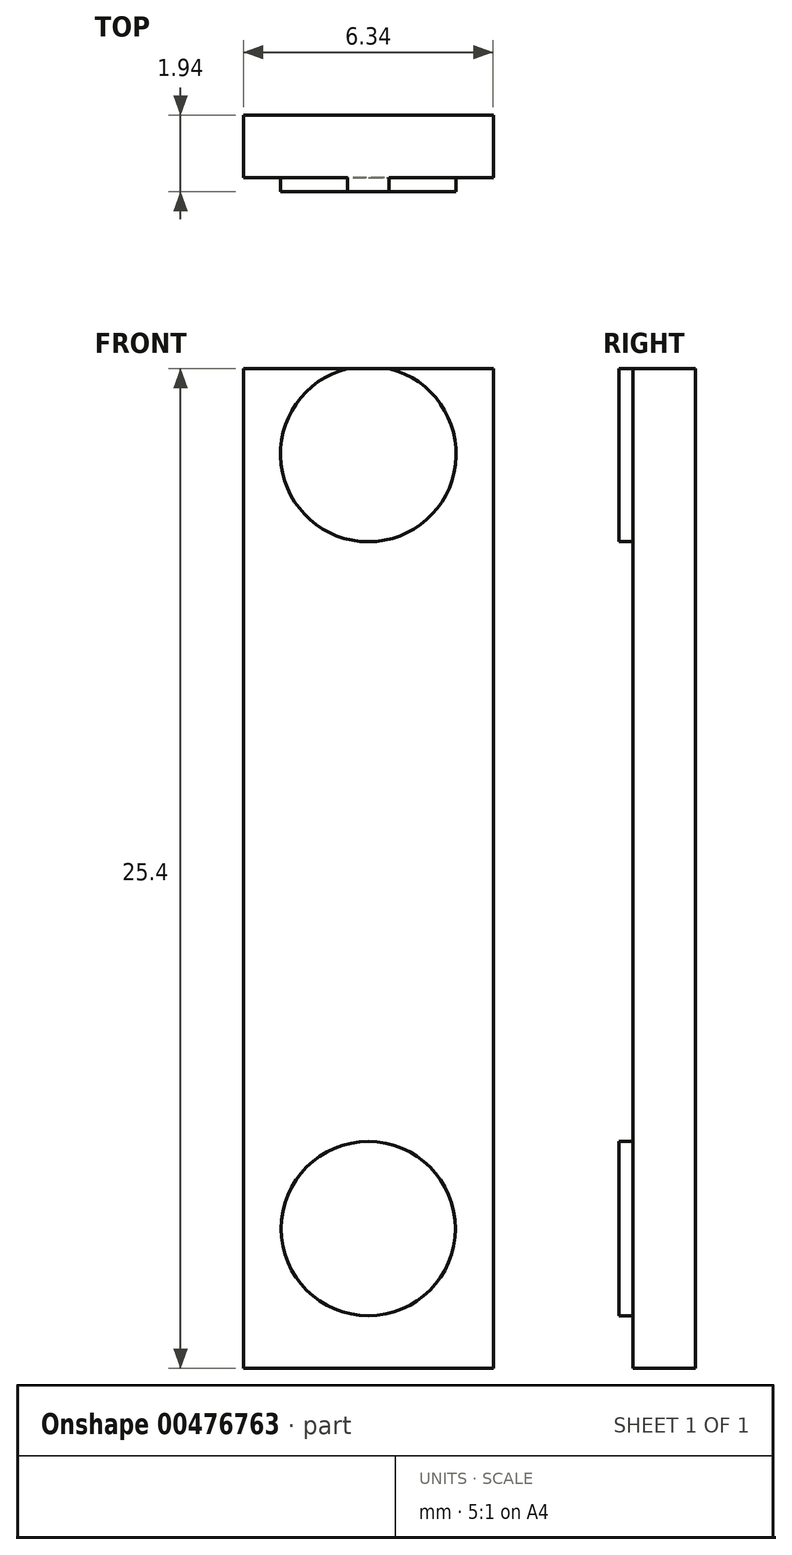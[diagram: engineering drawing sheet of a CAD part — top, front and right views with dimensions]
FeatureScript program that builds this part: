
annotation { "Feature Type Name" : "Feature", "Feature Type Description" : "" }
export const myFeature = defineFeature(function(context is Context, id is Id, definition is map)
    precondition{}
    {
        {
            var Q0;
            Q0=qCreatedBy(makeId("Front.planeOp"),FACE);
            var sketch = newSketch(context, id + "F0", { "sketchPlane" : qUnion([Q0])});
            skLineSegment(sketch, "E0.bottom", {"start": v(3.17, -12.7) * mm, "end": v(-3.18, -12.7) * mm});
            skLineSegment(sketch, "E0.top", {"start": v(3.18, 12.7) * mm, "end": v(-3.17, 12.7) * mm});
            skLineSegment(sketch, "E0.left", {"start": v(3.17, -12.7) * mm, "end": v(3.18, 12.7) * mm});
            skLineSegment(sketch, "E0.right", {"start": v(-3.18, -12.7) * mm, "end": v(-3.17, 12.7) * mm});
            skPoint(sketch, "E0.middle", {"position": v(0, 0) * mm});
            skSolve(sketch);
        }
        {
            var Q0;
            Q0=makeQuery(id+"F0.imprint","IMPRINT",FACE,{"disambiguationData":[TD([[makeQuery(id+"F0.imprint","IMPRINT",EDGE,{"derivedFrom":sQuery(id+"F0.wireOp",EDGE,"E0.bottom")}),-1.0]])]});
            extrude(context, id + "F1", {"entities" : qUnion([Q0]), "depth" : 1.59 * mm});
        }
        {
            var Q0;
            Q0=makeQuery(id+"F1.opExtrude","CAP_FACE",FACE,{"disambiguationData":[OSD([sQuery(id+"F0.wireOp",EDGE,"E0.bottom"),sQuery(id+"F0.wireOp",EDGE,"E0.top"),sQuery(id+"F0.wireOp",EDGE,"E0.left"),sQuery(id+"F0.wireOp",EDGE,"E0.right")])],"isStart":false});
            var sketch = newSketch(context, id + "F2", { "sketchPlane" : qUnion([Q0])});
            skCircle(sketch, "E1", {"center": v(0, -9.15) * mm, "radius": 2.21 * mm});
            skCircle(sketch, "E2", {"center": v(0, 10.53) * mm, "radius": 2.23 * mm});
            skSolve(sketch);
        }
        {
            var Q0;
            Q0=makeQuery(id+"F2.imprint","IMPRINT",FACE,{"disambiguationData":[TD([[makeQuery(id+"F2.imprint","IMPRINT",EDGE,{"derivedFrom":sQuery(id+"F2.wireOp",EDGE,"E1")}),1.0]])]});
            var Q1;
            {var subQ0=sQuery(id+"F2.wireOp",EDGE,"E2");var subQ1=makeQuery(id+"F1.opExtrude","CAP_EDGE",EDGE,{"disambiguationData":[OSD([sQuery(id+"F0.wireOp",EDGE,"E0.top")])],"isStart":false});var subQ2=makeQuery(id+"F2.imprint","INTERSECT",VERTEX,{"disambiguationData":[OD(0.0)],"derivedFrom":[subQ1,subQ0]});Q1=makeQuery(id+"F2.imprint","IMPRINT",FACE,{"disambiguationData":[TD([[makeQuery(id+"F2.imprint","IMPRINT",EDGE,{"disambiguationData":[TD([[subQ2,1.0]])],"derivedFrom":subQ0}),1.0]])]});}
            extrude(context, id + "F3", {"entities" : qUnion([Q0, Q1]), "operationType" : NewBodyOperationType.ADD, "depth" : 0.36 * mm});
        }
    });
